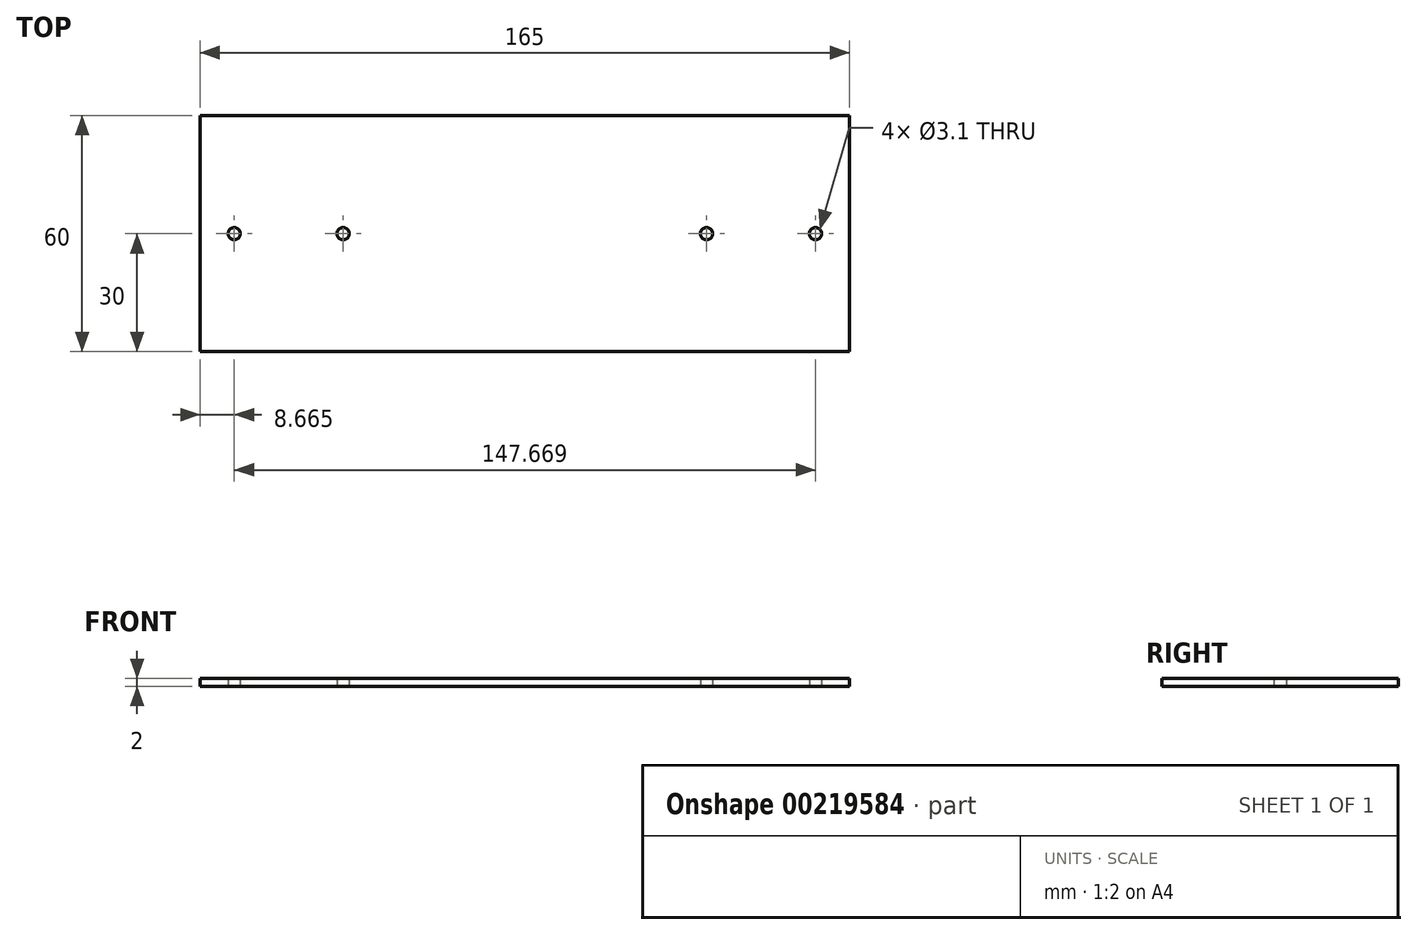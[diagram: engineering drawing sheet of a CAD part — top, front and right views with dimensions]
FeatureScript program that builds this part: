
annotation { "Feature Type Name" : "Feature", "Feature Type Description" : "" }
export const myFeature = defineFeature(function(context is Context, id is Id, definition is map)
    precondition{}
    {
        {
            var Q0;
            Q0=qCreatedBy(makeId("Top.planeOp"),FACE);
            var sketch = newSketch(context, id + "F0", { "sketchPlane" : qUnion([Q0])});
            skLineSegment(sketch, "E0.bottom", {"start": v(82.5, -30) * mm, "end": v(-82.5, -30) * mm});
            skLineSegment(sketch, "E0.top", {"start": v(82.5, 30) * mm, "end": v(-82.5, 30) * mm});
            skLineSegment(sketch, "E0.left", {"start": v(82.5, -30) * mm, "end": v(82.5, 30) * mm});
            skLineSegment(sketch, "E0.right", {"start": v(-82.5, -30) * mm, "end": v(-82.5, 30) * mm});
            skPoint(sketch, "E0.middle", {"position": v(0, 0) * mm});
            skCircle(sketch, "E1", {"center": v(73.83, 0) * mm, "radius": 1.55 * mm});
            skCircle(sketch, "E2", {"center": v(-73.83, 0) * mm, "radius": 1.55 * mm});
            skLineSegment(sketch, "E3", {"start": v(73.83, 0) * mm, "end": v(73.83, -30) * mm, "construction": true});
            skLineSegment(sketch, "E4", {"start": v(-73.83, 0) * mm, "end": v(-46.17, 0) * mm, "construction": true});
            skLineSegment(sketch, "E5", {"start": v(73.83, 0) * mm, "end": v(46.17, 0) * mm, "construction": true});
            skCircle(sketch, "E6", {"center": v(-46.17, 0) * mm, "radius": 1.55 * mm});
            skCircle(sketch, "E7", {"center": v(46.17, 0) * mm, "radius": 1.55 * mm});
            skLineSegment(sketch, "E8", {"start": v(73.83, 0) * mm, "end": v(73.83, 30) * mm, "construction": true});
            skSolve(sketch);
        }
        {
            var Q0;
            Q0=qSketchRegion(id+"F0",true);
            extrude(context, id + "F1", {"entities" : qUnion([Q0]), "depth" : 2 * mm});
        }
    });
